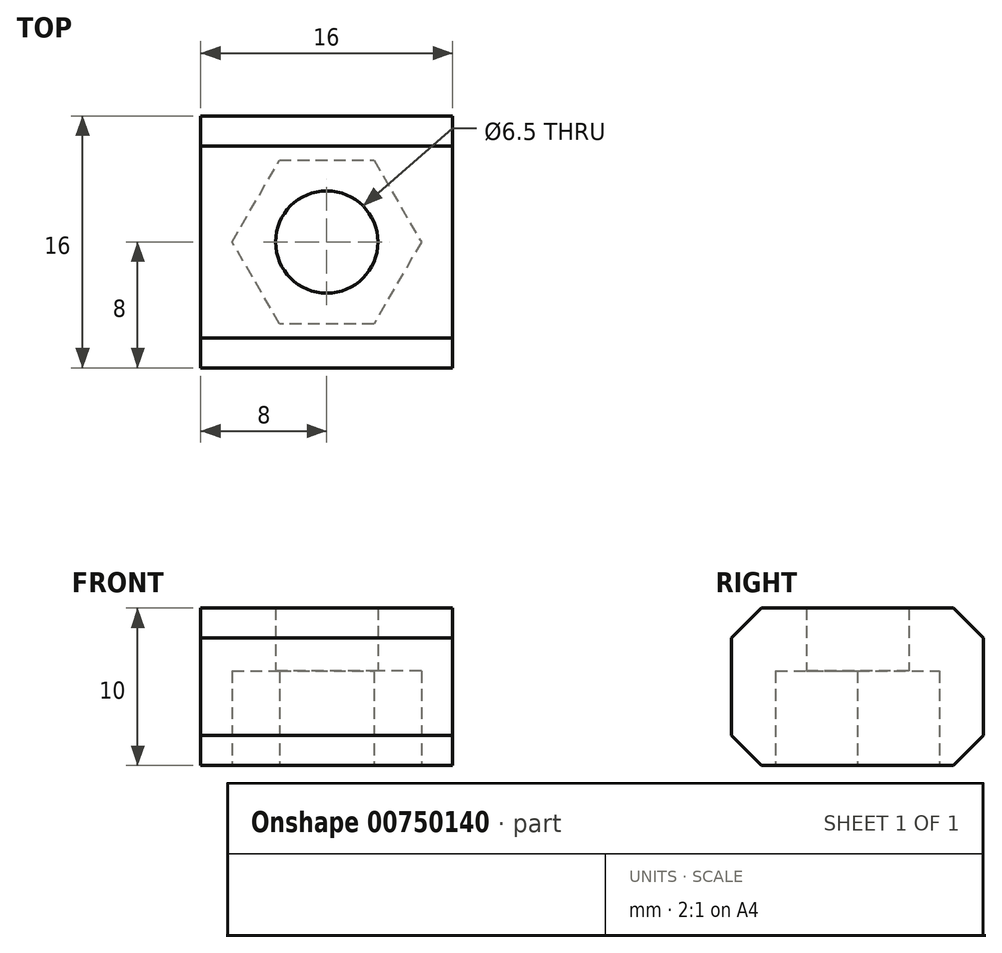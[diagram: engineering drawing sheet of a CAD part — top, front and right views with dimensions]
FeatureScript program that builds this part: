
annotation { "Feature Type Name" : "Feature", "Feature Type Description" : "" }
export const myFeature = defineFeature(function(context is Context, id is Id, definition is map)
    precondition{}
    {
        {
            var Q0;
            Q0=qCreatedBy(makeId("Top.planeOp"),FACE);
            var sketch = newSketch(context, id + "F0", { "sketchPlane" : qUnion([Q0])});
            skCircle(sketch, "E0.cCircle", {"center": v(0, 0) * mm, "radius": 5.2 * mm, "construction": true});
            skLineSegment(sketch, "E0.0", {"start": v(-3, 5.2) * mm, "end": v(3, 5.2) * mm});
            skLineSegment(sketch, "E0.1", {"start": v(3, 5.2) * mm, "end": v(6, 0) * mm});
            skLineSegment(sketch, "E0.2", {"start": v(6, 0) * mm, "end": v(3, -5.2) * mm});
            skLineSegment(sketch, "E0.3", {"start": v(3, -5.2) * mm, "end": v(-3, -5.2) * mm});
            skLineSegment(sketch, "E0.4", {"start": v(-3, -5.2) * mm, "end": v(-6, 0) * mm});
            skLineSegment(sketch, "E0.5", {"start": v(-6, 0) * mm, "end": v(-3, 5.2) * mm});
            skPoint(sketch, "E0.0.midPoint", {"position": v(0, 5.2) * mm});
            skLineSegment(sketch, "E1.bottom", {"start": v(8, 8) * mm, "end": v(-8, 8) * mm});
            skLineSegment(sketch, "E1.top", {"start": v(8, -8) * mm, "end": v(-8, -8) * mm});
            skLineSegment(sketch, "E1.left", {"start": v(8, 8) * mm, "end": v(8, -8) * mm});
            skLineSegment(sketch, "E1.right", {"start": v(-8, 8) * mm, "end": v(-8, -8) * mm});
            skCircle(sketch, "E2", {"center": v(0, 0) * mm, "radius": 3.25 * mm});
            skSolve(sketch);
        }
        {
            var Q0;
            Q0=makeQuery(id+"F0.imprint","IMPRINT",FACE,{"disambiguationData":[TD([[makeQuery(id+"F0.imprint","IMPRINT",EDGE,{"derivedFrom":sQuery(id+"F0.wireOp",EDGE,"E0.0")}),1.0]])]});
            var Q1;
            Q1=makeQuery(id+"F0.imprint","IMPRINT",FACE,{"disambiguationData":[TD([[makeQuery(id+"F0.imprint","IMPRINT",EDGE,{"derivedFrom":sQuery(id+"F0.wireOp",EDGE,"E0.0")}),-1.0]])]});
            extrude(context, id + "F1", {"entities" : qUnion([Q0, Q1]), "depth" : 10 * mm, "offsetDistance" : 25 * mm});
        }
        {
            var Q0;
            Q0=makeQuery(id+"F0.imprint","IMPRINT",FACE,{"disambiguationData":[TD([[makeQuery(id+"F0.imprint","IMPRINT",EDGE,{"derivedFrom":sQuery(id+"F0.wireOp",EDGE,"E0.0")}),-1.0]])]});
            extrude(context, id + "F2", {"entities" : qUnion([Q0]), "operationType" : NewBodyOperationType.REMOVE, "depth" : 6 * mm, "offsetDistance" : 25 * mm});
        }
        {
            var Q0;
            Q0=makeQuery(id+"F1.opExtrude","CAP_EDGE",EDGE,{"disambiguationData":[OSD([sQuery(id+"F0.wireOp",EDGE,"E1.bottom")])],"isStart":true});
            var Q1;
            Q1=makeQuery(id+"F1.opExtrude","CAP_EDGE",EDGE,{"disambiguationData":[OSD([sQuery(id+"F0.wireOp",EDGE,"E1.top")])],"isStart":true});
            var Q2;
            Q2=makeQuery(id+"F1.opExtrude","CAP_EDGE",EDGE,{"disambiguationData":[OSD([sQuery(id+"F0.wireOp",EDGE,"E1.bottom")])],"isStart":false});
            var Q3;
            Q3=makeQuery(id+"F1.opExtrude","CAP_EDGE",EDGE,{"disambiguationData":[OSD([sQuery(id+"F0.wireOp",EDGE,"E1.top")])],"isStart":false});
            chamfer(context, id + "F3", {"entities" : qUnion([Q0, Q1, Q2, Q3]), "width" : 1.9 * mm, "tangentPropagation" : true});
        }
    });
